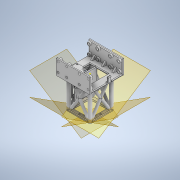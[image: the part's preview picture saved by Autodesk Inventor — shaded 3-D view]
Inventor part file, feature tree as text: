
AUTODESK INVENTOR PART (.ipt)
format: ipt  version: 2020 (Build 240168000, 168)  size: 963,584 bytes
history: native  units: in
note: dims shown in document units (in); Inventor stores cm internally (conversion verified against a paired STEP export)
features: sketch x22, extrude x21, plane x8, mirror x4, fillet x4, chamfer x2, pattern_circular x1
ambient origin geometry x8: Origin, YZ Plane, XZ Plane, XY Plane, X Axis, Y Axis, Z Axis, Center Point
bodies: Solid1 (feature_tree)
feature tree (62):
  extrude  "Extrusion1"  Depth=0.1969in TaperAngle=0.0deg
  extrude  "Extrusion2"  Depth=0.1969in
  extrude  "Extrusion3"  Depth=2.0079in
  extrude  "Extrusion4"  Depth=0.2362in
  mirror  "Mirror1"
  mirror  "Mirror2"
  extrude  "Extrusion5"  Depth=0.2362in
  extrude  "Extrusion6"  Depth=5.9055in TaperAngle=0.0deg
  extrude  "Extrusion7"  Depth=0.3937in
  sketch  "Sketch8"  dims[d18=0.3937in d19=0.3937in d20=0.3937in d21=0.0in]
  extrude  "Extrusion8"  Depth=0.3937in
  chamfer  "Chamfer1"  Distance=0.3937in
  mirror  "Mirror3"
  extrude  "Extrusion9"  Depth=0.0591in
  extrude  "Extrusion10"  Depth=0.0591in
  plane  "Work Plane1"
  extrude  "Extrusion11"  TaperAngle=135.0deg  [1 undecoded]
  mirror  "Mirror4"
  pattern_circular  "Circular Pattern1"  [2 undecoded]
  extrude  "Extrusion12"  Depth=1.7717in
  extrude  "Extrusion13"  Depth=1.7717in
  fillet  "Fillet1"  Radius=0.8268in
  extrude  "Extrusion14"  Depth=1.7717in
  fillet  "Fillet2"  Radius=0.3937in
  fillet  "Fillet3"  Radius=0.1969in
  extrude  "Extrusion15"  Depth=1.7717in
  extrude  "Extrusion16"  Depth=1.7717in
  extrude  "Extrusion17"  Depth=1.7717in TaperAngle=0.0deg
  extrude  "Extrusion18"  Depth=1.7717in TaperAngle=45.0deg
  extrude  "Extrusion19"  Depth=1.7717in
  extrude  "Extrusion20"  Depth=1.7717in
  fillet  "Fillet4"  Radius=0.3937in
  chamfer  "Chamfer2"  Distance=0.3937in
  extrude  "Extrusion21"  Depth=1.7717in TaperAngle=0.0deg
  sketch  "Sketch1"  dims[d1=4.0157in d2=0.1969in d3=0.0in]
  sketch  "Sketch2"  dims[d4=0.1969in d5=0.1969in]
  sketch  "Sketch3"  dims[d6=1.5748in d7=0.0in d8=2.0079in]
  sketch  "Sketch4"  dims[d9=2.0079in d10=0.2362in]
  sketch  "Sketch5"  dims[d11=0.2362in d12=0.2362in]
  sketch  "Sketch6"  dims[d13=0.2362in d14=5.9055in d15=0.0in]
  sketch  "Sketch7"  dims[d16=0.3937in d17=0.3937in]
  sketch  "Sketch9"  dims[d23=0.1969in d24=0.0591in]
  sketch  "Sketch10"  dims[d25=45.0deg d26=0.0591in]
  sketch  "Sketch11"  dims[d27=90.0deg d28=135.0deg]
  sketch  "Sketch12"  dims[d29=0.0591in]
  plane  "Work Plane2"
  plane  "Work Plane3"
  plane  "Work Plane4"
  plane  "Work Plane5"
  plane  "Work Plane6"
  plane  "Work Plane7"
  plane  "Work Plane8"
  sketch  "Sketch13"  dims[d30=45.0deg]
  sketch  "Sketch14"  dims[d31=0.0591in]
  sketch  "Sketch15"  dims[d32=90.0deg]
  sketch  "Sketch16"  dims[d33=0.0591in]
  sketch  "Sketch17"  dims[d34=90.0deg]
  sketch  "Sketch18"  dims[d35=90.0deg]
  sketch  "Sketch19"  dims[d36=0.9843in d37=0.0in]
  sketch  "Sketch20"  dims[d38=0.0in]
  sketch  "Sketch21"  dims[d39=0.8268in d40=0.0in]
  sketch  "Sketch22"  dims[d41=0.4134in d42=0.4134in d43=0.1575in d44=0.1575in d45=0.8268in d46=0.0in d47=0.1969in d48=0.3937in d49=0.1969in d50=0.3937in d51=0.1969in d52=0.3937in d53=0.0in d54=0.3937in d55=0.0787in d56=45.0deg d58=0.3937in d59=0.3937in d60=0.3937in d61=0.3937in d62=3.7402in d63=0.0in d64=0.748in d65=0.748in d66=0.748in d67=0.748in d68=0.3937in d69=0.1969in d70=0.0in d71=0.2233in d72=0.2953in d73=4.0551in d74=0.0984in d75=0.0in d76=0.0in d77=1.5748in d78=360.0deg d80=4.0551in d81=0.0in d82=0.1575in d83=0.1575in d84=0.1575in d85=0.1575in d86=0.3937in d87=0.0in d88=0.0787in d89=0.1969in d90=0.3937in d91=0.5906in d92=0.0984in d93=0.0in d94=0.0in d95=0.0787in d96=0.1181in d97=0.6693in d98=0.6693in d99=0.1575in d100=0.1575in d101=0.9843in d102=0.0in d103=1.7717in d104=1.7717in d105=1.9685in d106=0.0in d107=1.7717in d108=1.7717in d109=2.1654in d110=2.1654in d111=1.2992in d112=0.0in d113=1.7717in d114=1.7717in d115=2.1654in d116=2.1654in d117=1.1024in d118=0.0in d119=0.1969in d120=2.5197in d121=0.1969in d122=2.5197in d123=2.5591in d124=0.0in d125=0.9449in d126=0.1575in d127=0.1575in d128=0.1575in d129=0.1575in d130=0.3937in d131=0.0in d132=0.0787in d133=0.0787in d134=0.0787in d135=45.0deg d136=0.0787in d137=0.0in]
note: 3 required parameter values undecoded (feature->parameter linkage not recoverable at this tier; creation-order binding heuristic only, values carry confidence <= 0.55)
